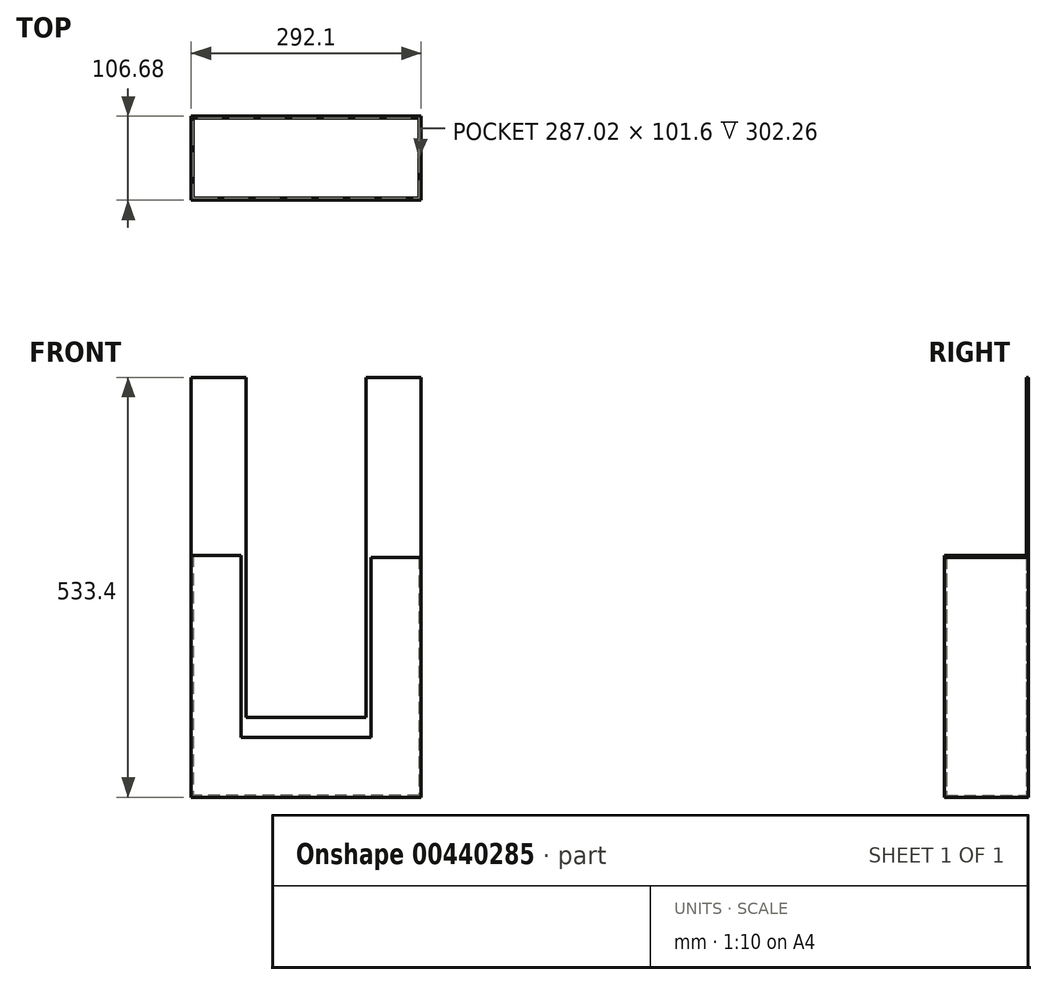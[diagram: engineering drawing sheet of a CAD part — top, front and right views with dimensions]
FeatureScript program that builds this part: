
annotation { "Feature Type Name" : "Feature", "Feature Type Description" : "" }
export const myFeature = defineFeature(function(context is Context, id is Id, definition is map)
    precondition{}
    {
        {
            var Q0;
            Q0=qCreatedBy(makeId("Front.planeOp"),FACE);
            var sketch = newSketch(context, id + "F0", { "sketchPlane" : qUnion([Q0])});
            skLineSegment(sketch, "E0.bottom", {"start": v(146.05, 139.7) * mm, "end": v(-146.05, 139.7) * mm});
            skLineSegment(sketch, "E0.top", {"start": v(146.05, -139.7) * mm, "end": v(-146.05, -139.7) * mm});
            skLineSegment(sketch, "E0.left", {"start": v(146.05, 139.7) * mm, "end": v(146.05, -139.7) * mm});
            skLineSegment(sketch, "E0.right", {"start": v(-146.05, 139.7) * mm, "end": v(-146.05, -139.7) * mm});
            skPoint(sketch, "E0.middle", {"position": v(0, 0) * mm});
            skSolve(sketch);
        }
        {
            var Q0;
            Q0 = qSketchRegion(id + "F0", true);
            extrude(context, id + "F1", {"entities" : qUnion([Q0]), "oppositeDirection" : true, "depth" : 2.54 * mm});
        }
        {
            var Q0;
            Q0=makeQuery(id+"F1.opExtrude","SWEPT_BODY",BODY,{"disambiguationData":[OSD([sQuery(id+"F0.wireOp",EDGE,"E0.bottom"),sQuery(id+"F0.wireOp",EDGE,"E0.top"),sQuery(id+"F0.wireOp",EDGE,"E0.left"),sQuery(id+"F0.wireOp",EDGE,"E0.right")])]});
            var Q1;
            Q1=makeQuery(id+"F1.opExtrude","SWEPT_FACE",FACE,{"disambiguationData":[OSD([sQuery(id+"F0.wireOp",EDGE,"E0.bottom")])]});
            mirror(context, id + "F2", {"operationType" : NewBodyOperationType.ADD, "entities" : qUnion([Q0]), "mirrorPlane" : qUnion([Q1])});
        }
        {
            var Q0;
            {var subQ0=makeQuery(id+"F1.opExtrude","CAP_FACE",FACE,{"disambiguationData":[OSD([sQuery(id+"F0.wireOp",EDGE,"E0.bottom"),sQuery(id+"F0.wireOp",EDGE,"E0.top"),sQuery(id+"F0.wireOp",EDGE,"E0.left"),sQuery(id+"F0.wireOp",EDGE,"E0.right")])],"isStart":true});Q0=makeQuery(id+"F2.boolean.opBoolean","MERGE",FACE,{"derivedFrom":[subQ0,makeQuery(id+"F2.opPattern","COPY",FACE,{"derivedFrom":subQ0,"instanceName":"1"})]});}
            var sketch = newSketch(context, id + "F3", { "sketchPlane" : qUnion([Q0])});
            skLineSegment(sketch, "E1.0", {"start": v(-143.5, 419.1) * mm, "end": v(-143.5, -137.16) * mm});
            skLineSegment(sketch, "E1.1", {"start": v(143.5, -137.16) * mm, "end": v(-143.5, -137.16) * mm});
            skLineSegment(sketch, "E1.2", {"start": v(143.51, 419.1) * mm, "end": v(143.5, -137.16) * mm});
            skLineSegment(sketch, "E2", {"start": v(-143.5, 167.64) * mm, "end": v(-146.05, 167.64) * mm});
            skLineSegment(sketch, "E3", {"start": v(143.5, 165.1) * mm, "end": v(146.05, 165.1) * mm});
            skSolve(sketch);
        }
        {
            var Q0;
            {var subQ2=sQuery(id+"F3.wireOp",EDGE,"E1.1");Q0=makeQuery(id+"F3.imprint","IMPRINT",FACE,{"disambiguationData":[TD([[makeQuery(id+"F3.imprint","IMPRINT",EDGE,{"derivedFrom":subQ2}),1.0]])]});}
            extrude(context, id + "F4", {"entities" : qUnion([Q0]), "operationType" : NewBodyOperationType.ADD, "depth" : 101.6 * mm});
        }
        {
            var Q0;
            Q0=makeQuery(id+"F4.opExtrude","CAP_FACE",FACE,{"disambiguationData":[OSD([sQuery(id+"F0.wireOp",EDGE,"E0.top"),sQuery(id+"F0.wireOp",EDGE,"E0.left"),sQuery(id+"F0.wireOp",EDGE,"E0.right"),sQuery(id+"F3.wireOp",EDGE,"E1.0"),sQuery(id+"F3.wireOp",EDGE,"E1.1"),sQuery(id+"F3.wireOp",EDGE,"E1.2"),sQuery(id+"F3.wireOp",EDGE,"E2"),sQuery(id+"F3.wireOp",EDGE,"E3")])],"isStart":false});
            var sketch = newSketch(context, id + "F5", { "sketchPlane" : qUnion([Q0])});
            skLineSegment(sketch, "E4.bottom", {"start": v(-146.05, 167.64) * mm, "end": v(-82.55, 167.64) * mm});
            skLineSegment(sketch, "E4.top", {"start": v(-146.05, -139.7) * mm, "end": v(-82.55, -139.7) * mm});
            skLineSegment(sketch, "E4.left", {"start": v(-146.05, 167.64) * mm, "end": v(-146.05, -139.7) * mm});
            skLineSegment(sketch, "E4.right", {"start": v(-82.55, 167.64) * mm, "end": v(-82.55, -139.7) * mm});
            skLineSegment(sketch, "E5.bottom", {"start": v(-146.05, -139.7) * mm, "end": v(146.05, -139.7) * mm});
            skLineSegment(sketch, "E5.top", {"start": v(-146.05, -63.5) * mm, "end": v(146.05, -63.5) * mm});
            skLineSegment(sketch, "E5.left", {"start": v(-146.05, -139.7) * mm, "end": v(-146.05, -63.5) * mm});
            skLineSegment(sketch, "E5.right", {"start": v(146.05, -139.7) * mm, "end": v(146.05, -63.5) * mm});
            skLineSegment(sketch, "E6.bottom", {"start": v(146.05, 165.1) * mm, "end": v(82.55, 165.1) * mm});
            skLineSegment(sketch, "E6.top", {"start": v(146.05, -139.7) * mm, "end": v(82.55, -139.7) * mm});
            skLineSegment(sketch, "E6.left", {"start": v(146.05, 165.1) * mm, "end": v(146.05, -139.7) * mm});
            skLineSegment(sketch, "E6.right", {"start": v(82.55, 165.1) * mm, "end": v(82.55, -139.7) * mm});
            skSolve(sketch);
        }
        {
            var Q0;
            Q0 = qSketchRegion(id + "F5", true);
            extrude(context, id + "F6", {"entities" : qUnion([Q0]), "operationType" : NewBodyOperationType.ADD, "depth" : 2.54 * mm});
        }
        {
            var Q0;
            Q0=makeQuery(id+"F2.opPattern","COPY",FACE,{"derivedFrom":makeQuery(id+"F1.opExtrude","SWEPT_FACE",FACE,{"disambiguationData":[OSD([sQuery(id+"F0.wireOp",EDGE,"E0.top")])]}),"instanceName":"1"});
            var sketch = newSketch(context, id + "F7", { "sketchPlane" : qUnion([Q0])});
            skLineSegment(sketch, "E7.bottom", {"start": v(146.05, 2.54) * mm, "end": v(-146.05, 2.54) * mm});
            skLineSegment(sketch, "E7.top", {"start": v(146.05, 0) * mm, "end": v(-146.05, 0) * mm});
            skLineSegment(sketch, "E7.left", {"start": v(146.05, 2.54) * mm, "end": v(146.05, 0) * mm});
            skLineSegment(sketch, "E7.right", {"start": v(-146.05, 2.54) * mm, "end": v(-146.05, 0) * mm});
            skSolve(sketch);
        }
        {
            var Q0;
            Q0 = qSketchRegion(id + "F7", true);
            extrude(context, id + "F8", {"entities" : qUnion([Q0]), "operationType" : NewBodyOperationType.REMOVE, "oppositeDirection" : true, "depth" : 25.4 * mm});
        }
        {
            var Q0;
            {var subQ0=makeQuery(id+"F1.opExtrude","CAP_FACE",FACE,{"disambiguationData":[OSD([sQuery(id+"F0.wireOp",EDGE,"E0.bottom"),sQuery(id+"F0.wireOp",EDGE,"E0.top"),sQuery(id+"F0.wireOp",EDGE,"E0.left"),sQuery(id+"F0.wireOp",EDGE,"E0.right")])],"isStart":true});Q0=makeQuery(id+"F2.boolean.opBoolean","MERGE",FACE,{"derivedFrom":[subQ0,makeQuery(id+"F2.opPattern","COPY",FACE,{"derivedFrom":subQ0,"instanceName":"1"})]});}
            var sketch = newSketch(context, id + "F9", { "sketchPlane" : qUnion([Q0])});
            skLineSegment(sketch, "E8.bottom", {"start": v(-76.2, 393.7) * mm, "end": v(76.2, 393.7) * mm});
            skLineSegment(sketch, "E8.top", {"start": v(-76.2, -38.1) * mm, "end": v(76.2, -38.1) * mm});
            skLineSegment(sketch, "E8.left", {"start": v(-76.2, 393.7) * mm, "end": v(-76.2, -38.1) * mm});
            skLineSegment(sketch, "E8.right", {"start": v(76.2, 393.7) * mm, "end": v(76.2, -38.1) * mm});
            skSolve(sketch);
        }
        {
            var Q0;
            Q0 = qSketchRegion(id + "F9", true);
            extrude(context, id + "F10", {"entities" : qUnion([Q0]), "operationType" : NewBodyOperationType.REMOVE, "oppositeDirection" : true, "depth" : 25.4 * mm});
        }
    });
